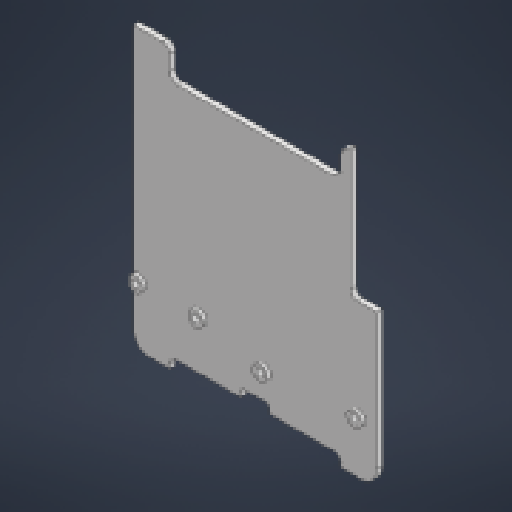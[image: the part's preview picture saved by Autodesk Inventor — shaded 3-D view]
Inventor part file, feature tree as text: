
AUTODESK INVENTOR PART (.ipt)
format: ipt  version: 2025 (Build 290162000, 162)  size: 316,416 bytes
history: native  units: mm
features: extrude x7, sketch x7, projected_geometry x5, fillet x3, other x3, reference x1
ambient origin geometry x8: Origin, YZ Plane, XZ Plane, XY Plane, X Axis, Y Axis, Z Axis, Center Point
bodies: 实体1 (feature_tree)
feature tree (26):
  extrude  "拉伸1"  Depth=1.5mm
  extrude  "拉伸2"  Depth=1.0mm
  fillet  "圆角1"  Radius=10.0mm
  extrude  "拉伸3"  Depth=7.0mm
  fillet  "圆角2"  Radius=32.0mm
  extrude  "拉伸4"  Depth=10.0mm TaperAngle=0.0deg
  extrude  "拉伸5"  Depth=2.0mm
  fillet  "圆角3"  Radius=1.0mm
  extrude  "拉伸7"  Depth=1.0mm
  extrude  "拉伸8"  Depth=1.0mm TaperAngle=0.0deg
  sketch  "草图1"  dims[d0=1.5mm d1=0.0mm d3=3.0mm]
  sketch  "草图2"  dims[d4=2.0mm d5=0.0mm d6=1.0mm d7=10.0mm d8=0.0mm]
  sketch  "草图3"  dims[d9=1.0mm d10=7.0mm d11=32.0mm]
  reference  "参考2"
  sketch  "草图4"  dims[d12=10.0mm d13=0.0mm d14=10.0mm d15=0.0mm]
  projected_geometry  "投影回路1"
  sketch  "草图5"  dims[d16=8.0mm d17=2.0mm d20=1.0mm]
  sketch  "草图6"  dims[d21=1.0mm d22=1.0mm]
  sketch  "草图7"  dims[d23=1.0mm d24=1.0mm d25=0.0mm d26=7.0mm d27=0.0mm d28=25.0mm d29=17.0mm d30=16.0mm d33=9.008404mm d35=5.0mm d36=2.0mm d37=4.0mm]
  projected_geometry  "投影回路2"
  projected_geometry  "投影回路3"
  projected_geometry  "投影回路4"
  projected_geometry  "投影回路5"
  parser-record x1  (decoder bookkeeping rows leaked as tree rows — omitted from the tree; the rows remain in map.json)
  other  "装配体.iam"
  other  "键盘外壳:1"
note: 1 file-system path scrubbed to <path> (originals preserved in map.json)
